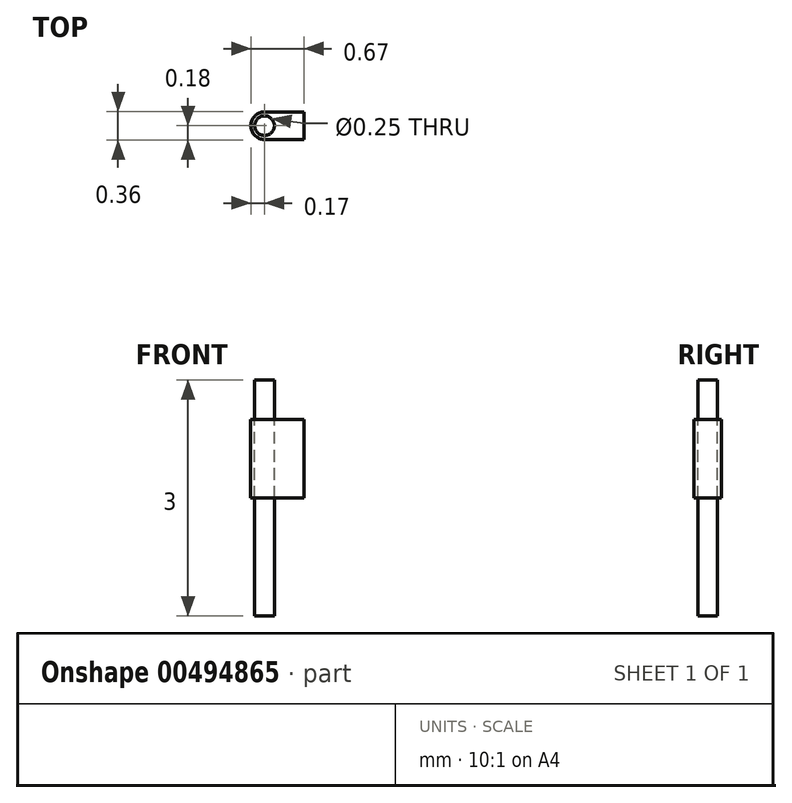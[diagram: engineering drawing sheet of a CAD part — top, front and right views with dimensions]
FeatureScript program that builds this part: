
annotation { "Feature Type Name" : "Feature", "Feature Type Description" : "" }
export const myFeature = defineFeature(function(context is Context, id is Id, definition is map)
    precondition{}
    {
        {
            var Q0;
            Q0=qCreatedBy(makeId("Top.planeOp"),FACE);
            var sketch = newSketch(context, id + "F0", { "sketchPlane" : qUnion([Q0])});
            skCircle(sketch, "E0", {"center": v(0, 0) * mm, "radius": 0.12 * mm});
            skArc(sketch, "E1", {"start": v(0, 0.17) * mm, "mid": v(-0.17, 0) * mm, "end": v(0, -0.17) * mm});
            skLineSegment(sketch, "E2", {"start": v(0, 0.17) * mm, "end": v(0.5, 0.17) * mm});
            skLineSegment(sketch, "E3", {"start": v(0.5, 0.17) * mm, "end": v(0.5, -0.17) * mm});
            skLineSegment(sketch, "E4", {"start": v(0, -0.17) * mm, "end": v(0.5, -0.17) * mm});
            skSolve(sketch);
        }
        {
            var Q0;
            Q0=makeQuery(id+"F0.imprint","IMPRINT",FACE,{"disambiguationData":[TD([[makeQuery(id+"F0.imprint","IMPRINT",EDGE,{"derivedFrom":sQuery(id+"F0.wireOp",EDGE,"E0")}),-1.0]])]});
            extrude(context, id + "F1", {"entities" : qUnion([Q0]), "depth" : 1 * mm});
        }
        {
            var Q0;
            Q0=makeQuery(id+"F0.imprint","IMPRINT",FACE,{"disambiguationData":[TD([[makeQuery(id+"F0.imprint","IMPRINT",EDGE,{"derivedFrom":sQuery(id+"F0.wireOp",EDGE,"E0")}),1.0]])]});
            extrude(context, id + "F2", {"entities" : qUnion([Q0]), "endBound" : BoundingType.SYMMETRIC, "oppositeDirection" : true, "depth" : 3 * mm});
        }
    });
